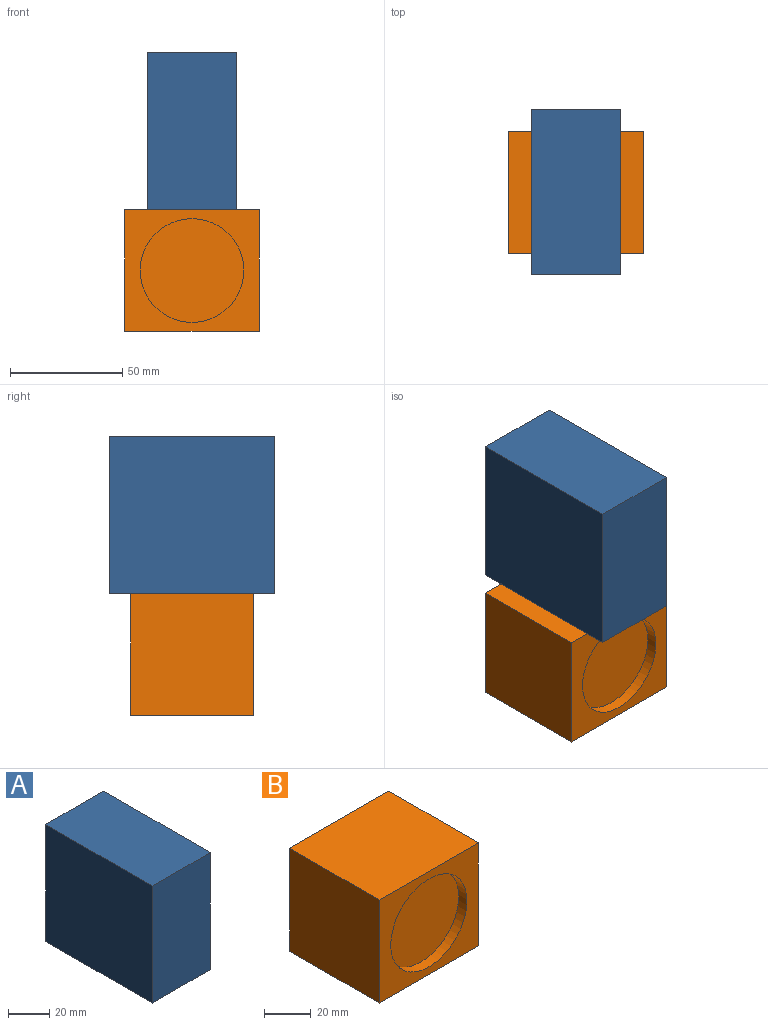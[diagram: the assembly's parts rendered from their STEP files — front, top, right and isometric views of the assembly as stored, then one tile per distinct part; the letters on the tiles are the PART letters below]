
ASSEMBLY  parts=2 mates=1
PART A: 6 faces, bbox 40x73.6x69.8 mm
  f0: plane 73.59x40mm, normal (0,0,1), area 2943.4mm2, adj f1,f3,f4,f5
  f1: plane 69.84x40mm, normal (0,-1,0), area 2793.6mm2, adj f0,f2,f4,f5
  f2: plane 73.59x40mm, normal (0,0,-1), area 2943.4mm2, adj f1,f3,f4,f5
  f3: plane 69.84x40mm, normal (0,1,0), area 2793.6mm2, adj f0,f2,f4,f5
  f4: plane 73.59x69.84mm, normal (1,0,0), area 5139.1mm2, adj f0,f1,f2,f3
  f5: plane 73.59x69.84mm, normal (-1,0,0), area 5139.1mm2, adj f0,f1,f2,f3
PART B: 8 faces, bbox 60x54.3x54 mm
  f0: plane 60x54.32mm, normal (0,0,1), area 3259mm2, adj f1,f3,f4,f5
  f1: plane 60x53.97mm, normal (0,-1,0), area 1569.2mm2, adj f0,f2,f4,f5,f6
  f2: plane 60x54.32mm, normal (0,0,-1), area 3259mm2, adj f1,f3,f4,f5
  f3: plane 60x53.97mm, normal (0,1,0), area 3238.3mm2, adj f0,f2,f4,f5
  f4: plane 54.32x53.97mm, normal (1,0,0), area 2931.6mm2, adj f0,f1,f2,f3
  f5: plane 54.32x53.97mm, normal (-1,0,0), area 2931.6mm2, adj f0,f1,f2,f3
  f6: cylinder r=23.05mm len=46.1mm, axis (0,-1,0), area 724.1mm2, adj f1,f7
  f7: plane 46.1x46.1mm, normal (0,-1,0), area 1669.1mm2, adj f6
PLACE A t=(-20,0,61.91)mm
PLACE B at identity fixed
MATE fastened B.f0 <-> A.f2  axis (0,0,1) through (0,0,26.99)mm
